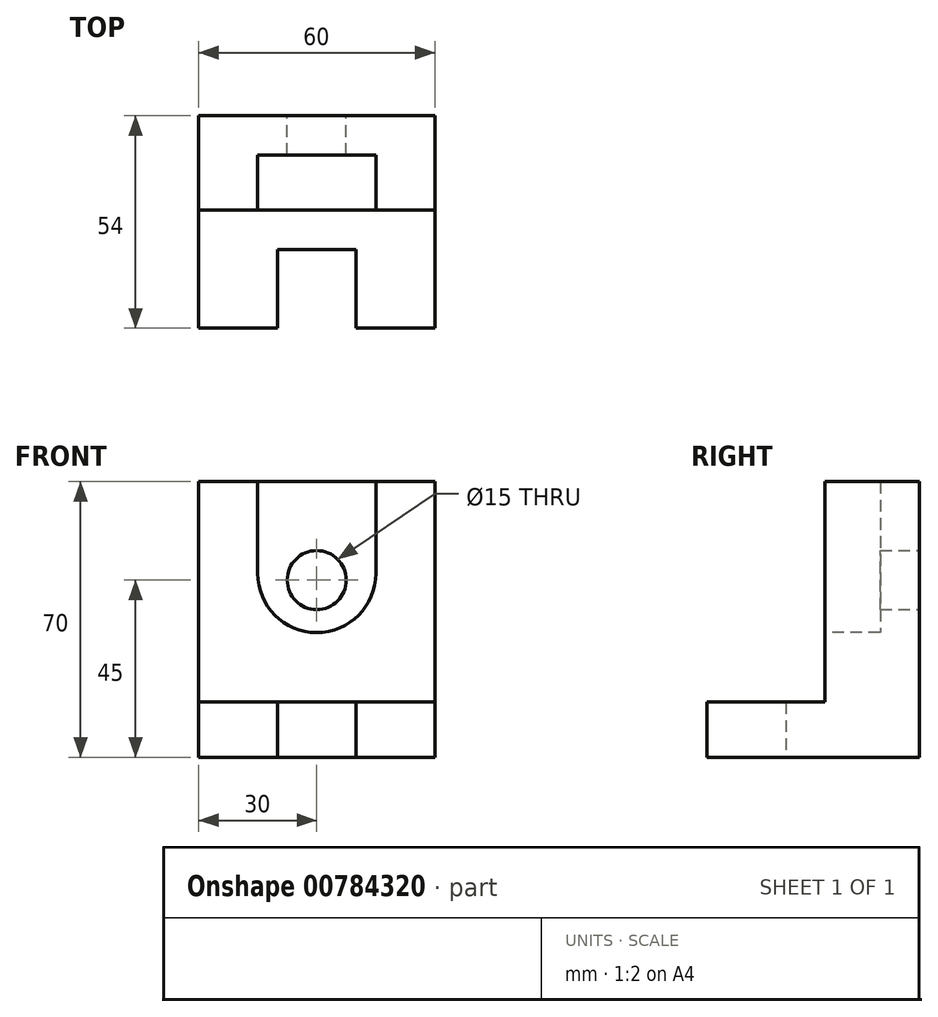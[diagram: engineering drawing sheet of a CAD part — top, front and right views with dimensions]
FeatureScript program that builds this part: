
annotation { "Feature Type Name" : "Feature", "Feature Type Description" : "" }
export const myFeature = defineFeature(function(context is Context, id is Id, definition is map)
    precondition{}
    {
        {
            var Q0;
            Q0=qCreatedBy(makeId("Front.planeOp"),FACE);
            var sketch = newSketch(context, id + "F0", { "sketchPlane" : qUnion([Q0])});
            skLineSegment(sketch, "E0.bottom", {"start": v(30, 35) * mm, "end": v(-30, 35) * mm});
            skLineSegment(sketch, "E0.top", {"start": v(30, -35) * mm, "end": v(-30, -35) * mm});
            skLineSegment(sketch, "E0.left", {"start": v(30, 35) * mm, "end": v(30, -35) * mm});
            skLineSegment(sketch, "E0.right", {"start": v(-30, 35) * mm, "end": v(-30, -35) * mm});
            skPoint(sketch, "E0.middle", {"position": v(0, 0) * mm});
            skSolve(sketch);
        }
        {
            var Q0;
            Q0=makeQuery(id+"F0.imprint","IMPRINT",FACE,{"disambiguationData":[TD([[makeQuery(id+"F0.imprint","IMPRINT",EDGE,{"derivedFrom":sQuery(id+"F0.wireOp",EDGE,"E0.bottom")}),1.0]])]});
            extrude(context, id + "F1", {"entities" : qUnion([Q0]), "depth" : 24 * mm, "offsetDistance" : 25 * mm});
        }
        {
            var Q0;
            Q0=makeQuery(id+"F1.opExtrude","CAP_FACE",FACE,{"disambiguationData":[OSD([sQuery(id+"F0.wireOp",EDGE,"E0.bottom"),sQuery(id+"F0.wireOp",EDGE,"E0.top"),sQuery(id+"F0.wireOp",EDGE,"E0.left"),sQuery(id+"F0.wireOp",EDGE,"E0.right")])],"isStart":false});
            var sketch = newSketch(context, id + "F2", { "sketchPlane" : qUnion([Q0])});
            skLineSegment(sketch, "E1", {"start": v(-15, 35) * mm, "end": v(-15, 11.65) * mm});
            skLineSegment(sketch, "E2", {"start": v(15, 11.65) * mm, "end": v(15, 35) * mm});
            skArc(sketch, "E3", {"start": v(-15, 11.65) * mm, "mid": v(0, -3.35) * mm, "end": v(15, 11.65) * mm});
            skSolve(sketch);
        }
        {
            var Q0;
            {var subQ0=sQuery(id+"F2.wireOp",EDGE,"E1");Q0=makeQuery(id+"F2.imprint","IMPRINT",FACE,{"disambiguationData":[TD([[makeQuery(id+"F2.imprint","IMPRINT",EDGE,{"derivedFrom":subQ0}),1.0]])]});}
            extrude(context, id + "F3", {"entities" : qUnion([Q0]), "operationType" : NewBodyOperationType.REMOVE, "oppositeDirection" : true, "depth" : 14 * mm, "offsetDistance" : 25 * mm});
        }
        {
            var Q0;
            Q0=makeQuery(id+"F1.opExtrude","CAP_FACE",FACE,{"disambiguationData":[OSD([sQuery(id+"F0.wireOp",EDGE,"E0.bottom"),sQuery(id+"F0.wireOp",EDGE,"E0.top"),sQuery(id+"F0.wireOp",EDGE,"E0.left"),sQuery(id+"F0.wireOp",EDGE,"E0.right")])],"isStart":true});
            var sketch = newSketch(context, id + "F4", { "sketchPlane" : qUnion([Q0])});
            skCircle(sketch, "E4", {"center": v(0, 10) * mm, "radius": 7.5 * mm});
            skPoint(sketch, "E5.orphan", {"position": v(-30, 10) * mm});
            skSolve(sketch);
        }
        {
            var Q0;
            Q0=makeQuery(id+"F4.imprint","IMPRINT",FACE,{"disambiguationData":[TD([[makeQuery(id+"F4.imprint","IMPRINT",EDGE,{"derivedFrom":sQuery(id+"F4.wireOp",EDGE,"E4")}),1.0]])]});
            extrude(context, id + "F5", {"entities" : qUnion([Q0]), "operationType" : NewBodyOperationType.REMOVE, "endBound" : BoundingType.THROUGH_ALL, "oppositeDirection" : true, "depth" : 25 * mm, "offsetDistance" : 25 * mm});
        }
        {
            var Q0;
            Q0=makeQuery(id+"F1.opExtrude","CAP_FACE",FACE,{"disambiguationData":[OSD([sQuery(id+"F0.wireOp",EDGE,"E0.bottom"),sQuery(id+"F0.wireOp",EDGE,"E0.top"),sQuery(id+"F0.wireOp",EDGE,"E0.left"),sQuery(id+"F0.wireOp",EDGE,"E0.right")])],"isStart":false});
            var sketch = newSketch(context, id + "F6", { "sketchPlane" : qUnion([Q0])});
            skLineSegment(sketch, "E6.bottom", {"start": v(-30, -35) * mm, "end": v(30, -35) * mm});
            skLineSegment(sketch, "E6.top", {"start": v(-30, -21) * mm, "end": v(30, -21) * mm});
            skLineSegment(sketch, "E6.left", {"start": v(-30, -35) * mm, "end": v(-30, -21) * mm});
            skLineSegment(sketch, "E6.right", {"start": v(30, -35) * mm, "end": v(30, -21) * mm});
            skSolve(sketch);
        }
        {
            var Q0;
            Q0=makeQuery(id+"F6.imprint","IMPRINT",FACE,{"disambiguationData":[TD([[makeQuery(id+"F6.imprint","IMPRINT",EDGE,{"derivedFrom":sQuery(id+"F6.wireOp",EDGE,"E6.bottom")}),-1.0]])]});
            extrude(context, id + "F7", {"entities" : qUnion([Q0]), "operationType" : NewBodyOperationType.ADD, "depth" : 30 * mm, "offsetDistance" : 25 * mm});
        }
        {
            var Q0;
            Q0=makeQuery(id+"F7.opExtrude","CAP_FACE",FACE,{"disambiguationData":[OSD([sQuery(id+"F6.wireOp",EDGE,"E6.bottom"),sQuery(id+"F6.wireOp",EDGE,"E6.top"),sQuery(id+"F6.wireOp",EDGE,"E6.left"),sQuery(id+"F6.wireOp",EDGE,"E6.right")])],"isStart":false});
            var sketch = newSketch(context, id + "F8", { "sketchPlane" : qUnion([Q0])});
            skSolve(sketch);
        }
        {
            var Q0;
            Q0=makeQuery(id+"F8.imprint","IMPRINT",FACE,{"disambiguationData":[TD([[makeQuery(id+"F8.imprint","IMPRINT",EDGE,{"derivedFrom":makeQuery(id+"F7.opExtrude","CAP_EDGE",EDGE,{"disambiguationData":[OSD([sQuery(id+"F6.wireOp",EDGE,"E6.bottom")])],"isStart":false})}),-1.0]])]});
            var sketch = newSketch(context, id + "F9", { "sketchPlane" : qUnion([Q0])});
            skLineSegment(sketch, "E7", {"start": v(-10, -20.94) * mm, "end": v(-10, -34.9) * mm});
            skLineSegment(sketch, "E8", {"start": v(10, -20.94) * mm, "end": v(10, -34.94) * mm});
            skLineSegment(sketch, "E9", {"start": v(-10, -20.94) * mm, "end": v(10, -20.94) * mm});
            skLineSegment(sketch, "E10", {"start": v(-10, -34.9) * mm, "end": v(10, -34.94) * mm});
            skSolve(sketch);
        }
        {
            var Q0;
            {var subQ0=sQuery(id+"F9.wireOp",EDGE,"E10");Q0=makeQuery(id+"F9.imprint","IMPRINT",FACE,{"disambiguationData":[TD([[makeQuery(id+"F9.imprint","IMPRINT",EDGE,{"derivedFrom":subQ0}),1.0]])]});}
            extrude(context, id + "F10", {"entities" : qUnion([Q0]), "operationType" : NewBodyOperationType.REMOVE, "oppositeDirection" : true, "depth" : 20 * mm, "offsetDistance" : 25 * mm});
        }
        {
            var Q0;
            Q0=makeQuery(id+"F10.boolean.opBoolean","COPY",FACE,{"derivedFrom":makeQuery(id+"F10.opExtrude","SWEPT_FACE",FACE,{"disambiguationData":[OSD([sQuery(id+"F9.wireOp",EDGE,"E10")])]})});
            extrude(context, id + "F11", {"entities" : qUnion([Q0]), "operationType" : NewBodyOperationType.REMOVE, "endBound" : BoundingType.THROUGH_ALL, "oppositeDirection" : true, "depth" : 25 * mm, "offsetDistance" : 25 * mm});
        }
    });
